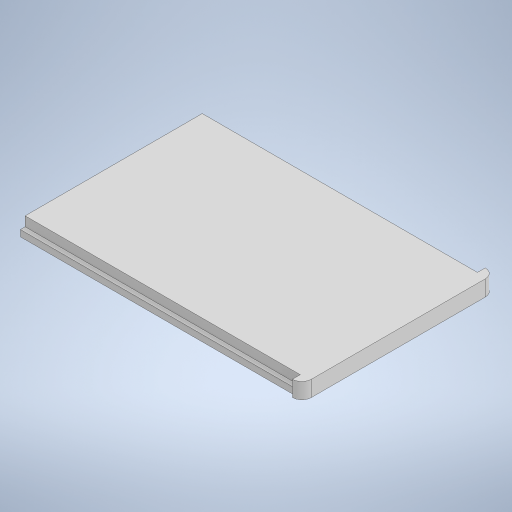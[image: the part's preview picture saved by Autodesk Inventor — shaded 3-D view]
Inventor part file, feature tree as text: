
AUTODESK INVENTOR PART (.ipt)
format: ipt  version: 2024.2 (Build 282272000, 272)  size: 218,624 bytes
history: native  units: mm
features: extrude x3, sketch x3, other x1
ambient origin geometry x8: Origin, YZ Plane, XZ Plane, XY Plane, X Axis, Y Axis, Z Axis, Center Point
bodies: Body1 (feature_tree)
feature tree (7):
  other  "Твердое тело1"
  extrude  "Выдавливание1"  Depth=87.0mm
  extrude  "Выдавливание2"  Depth=59.0mm
  extrude  "Выдавливание3"  Depth=2.0mm TaperAngle=0.0deg
  sketch  "Эскиз1"
  sketch  "Эскиз2"
  sketch  "Эскиз3"
